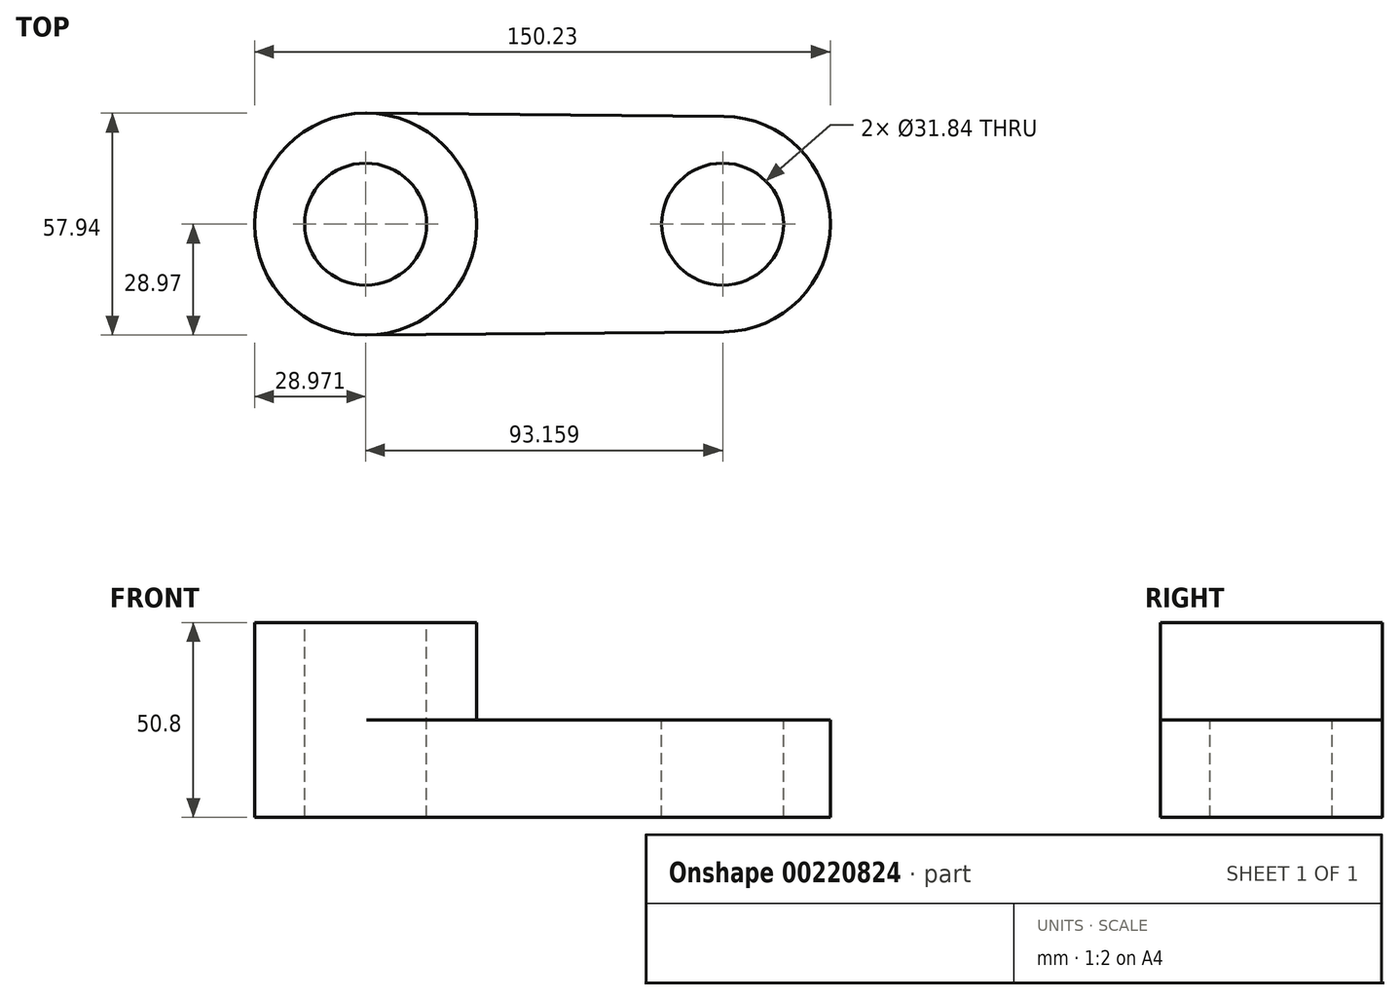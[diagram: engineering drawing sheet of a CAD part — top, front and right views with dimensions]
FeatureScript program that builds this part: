
annotation { "Feature Type Name" : "Feature", "Feature Type Description" : "" }
export const myFeature = defineFeature(function(context is Context, id is Id, definition is map)
    precondition{}
    {
        {
            var Q0;
            Q0=qCreatedBy(makeId("Top.planeOp"),FACE);
            var sketch = newSketch(context, id + "F0", { "sketchPlane" : qUnion([Q0])});
            skCircle(sketch, "E0", {"center": v(-46.58, 0) * mm, "radius": 15.92 * mm});
            skCircle(sketch, "E1", {"center": v(46.58, 0) * mm, "radius": 15.92 * mm});
            skArc(sketch, "E2", {"start": v(-46.3, 28.97) * mm, "mid": v(-75.55, 0) * mm, "end": v(-46.3, -28.97) * mm});
            skArc(sketch, "E3", {"start": v(46.84, -28.1) * mm, "mid": v(74.68, 0) * mm, "end": v(46.84, 28.1) * mm});
            skLineSegment(sketch, "E4", {"start": v(-46.3, 28.97) * mm, "end": v(46.84, 28.1) * mm});
            skLineSegment(sketch, "E5", {"start": v(46.84, -28.1) * mm, "end": v(-46.3, -28.97) * mm});
            skArc(sketch, "E6", {"start": v(-46.3, -28.97) * mm, "mid": v(-17.6, 0) * mm, "end": v(-46.3, 28.97) * mm});
            skSolve(sketch);
        }
        {
            var Q0;
            Q0=makeQuery(id+"F0.imprint","IMPRINT",FACE,{"disambiguationData":[TD([[makeQuery(id+"F0.imprint","IMPRINT",EDGE,{"derivedFrom":sQuery(id+"F0.wireOp",EDGE,"E1")}),-1.0]])]});
            var Q1;
            Q1=makeQuery(id+"F0.imprint","IMPRINT",FACE,{"disambiguationData":[TD([[makeQuery(id+"F0.imprint","IMPRINT",EDGE,{"derivedFrom":sQuery(id+"F0.wireOp",EDGE,"E0")}),-1.0]])]});
            extrude(context, id + "F1", {"entities" : qUnion([Q0, Q1]), "oppositeDirection" : true, "depth" : 25.4 * mm});
        }
        {
            var Q0;
            Q0=makeQuery(id+"F0.imprint","IMPRINT",FACE,{"disambiguationData":[TD([[makeQuery(id+"F0.imprint","IMPRINT",EDGE,{"derivedFrom":sQuery(id+"F0.wireOp",EDGE,"E0")}),-1.0]])]});
            extrude(context, id + "F2", {"entities" : qUnion([Q0]), "operationType" : NewBodyOperationType.ADD, "depth" : 25.4 * mm});
        }
    });
